# Revit family: Drain_Gutter_Zurn-Z575-Medium-Duty
name_source: partatom
category: Plumbing Fixtures
units: mm (PartAtom-declared; Revit-internal decimal feet)

## family parameters
Always vertical = Yes
Cut with Voids When Loaded = No
Maintain Annotation Orientation = No
OmniClass Number = 23.70.50.21.24.14
OmniClass Title = Deck Waste Water Drains
Part Type = Normal
Room Calculation Point = No
Round Connector Dimension = Use Radius
Shared = No
Work Plane-Based = No

## types (36) — shared parameters
Approx. Weight (Lbs) = 18 "
Assembly Code = D2030300
CW Connection = No
Default Elevation = 2 "
Description = 6 X 12 [152 X 305] MEDIUM-DUTY GUTTER DRAIN
Grate Open Area (Sq. In.) = 24 SF
HW Connection = No
Main Material = Iron - Zurn - Cast - Painted - Blue
Manufacturer = Zurn Water, LLC
Manufacurer Brand = Zurn
Model = Z575
Modified Date = 11/20/25
Product Documentation Link = https://files.zurn.com
Product Page URL = https://www.zurn.com
Product data url = https://www.bimobject.com
URL = www.zurn.com
Vent Connection = No
WFU = 1
Waste Connection = Yes
zero-valued in all types: CWFU, HWFU

## per-type parameters (varying)
| type | A_ Pipe Size (Inner Diameter) | A_ Pipe Size (Nominal Diameter) | A_ Pipe Size (Nominal Radius) | A_ Pipe Size (Outer Diameter) | Actual Body Height 'E' | Body Height 'E' | Grate Material | Thread length | Type Comments | Z1040-Adaptor Height | ZB/ZN | ZB/ZN Top |
| Z575-2IC | 2.067 " | 2 " | 1 " | 2.375 " | 5 " | 5 " | Iron - Zurn - Cast - Painted - Blue | 0 " | Z575 2 Inch Inside Caulk Outlet | 0 " | 0 " | No |
| Z575-3IC | 3.068 " | 3 " | 1.5 " | 3.5 " | 5 " | 5 " | Iron - Zurn - Cast - Painted - Blue | 0 " | Z575 3 Inch Inside Caulk Outlet | 0 " | 0 " | No |
| Z575-4IC | 4.026 " | 4 " | 2 " | 4.5 " | 5 " | 5 " | Iron - Zurn - Cast - Painted - Blue | 0 " | Z575 4 Inch Inside Caulk Outlet | 0 " | 0 " | No |
| ZB575-2IC | 2.067 " | 2 " | 1 " | 2.375 " | 5.188 " | 5 " | Bronze - Zurn - Polished | 0 " | ZB575 2 Inch Inside Caulk Outlet | 0 " | 0.188 " | Yes |
| ZB575-3IC | 3.068 " | 3 " | 1.5 " | 3.5 " | 5.188 " | 5 " | Bronze - Zurn - Polished | 0 " | ZB575 3 Inch Inside Caulk Outlet | 0 " | 0.188 " | Yes |
| ZB575-4IC | 4.026 " | 4 " | 2 " | 4.5 " | 5.188 " | 5 " | Bronze - Zurn - Polished | 0 " | ZB575 4 Inch Inside Caulk Outlet | 0 " | 0.188 " | Yes |
| ZN575-2IC | 2.067 " | 2 " | 1 " | 2.375 " | 5.188 " | 5 " | Bronze - Zurn - Polished Nickel | 0 " | ZN575 2 Inch Inside Caulk Outlet | 0 " | 0.188 " | Yes |
| ZN575-3IC | 3.068 " | 3 " | 1.5 " | 3.5 " | 5.188 " | 5 " | Bronze - Zurn - Polished Nickel | 0 " | ZN575 3 Inch Inside Caulk Outlet | 0 " | 0.188 " | Yes |
| ZN575-4IC | 4.026 " | 4 " | 2 " | 4.5 " | 5.188 " | 5 " | Bronze - Zurn - Polished Nickel | 0 " | ZN575 4 Inch Inside Caulk Outlet | 0 " | 0.188 " | Yes |
| Z575-2IP | 2.067 " | 2 " | 1 " | 2.375 " | 3.625 " | 3.625 " | Iron - Zurn - Cast - Painted - Blue | 0 " | Z575 2 Inch Threaded Outlet | 0 " | 0 " | No |
| Z575-3IP | 3.068 " | 3 " | 1.5 " | 3.5 " | 3.625 " | 3.625 " | Iron - Zurn - Cast - Painted - Blue | 0 " | Z575 3 Inch Threaded Outlet | 0 " | 0 " | No |
| Z575-4IP | 4.026 " | 4 " | 2 " | 4.5 " | 3.625 " | 3.625 " | Iron - Zurn - Cast - Painted - Blue | 0 " | Z575 4 Inch Threaded Outlet | 0 " | 0 " | No |
| ZB575-2IP | 2.067 " | 2 " | 1 " | 2.375 " | 3.813 " | 3.625 " | Bronze - Zurn - Polished | 0 " | ZB575 2 Inch Threaded Outlet | 0 " | 0.188 " | Yes |
| ZB575-3IP | 3.068 " | 3 " | 1.5 " | 3.5 " | 3.813 " | 3.625 " | Bronze - Zurn - Polished | 0 " | ZB575 3 Inch Threaded Outlet | 0 " | 0.188 " | Yes |
| ZB575-4IP | 4.026 " | 4 " | 2 " | 4.5 " | 3.813 " | 3.625 " | Bronze - Zurn - Polished | 0 " | ZB575 4 Inch Threaded Outlet | 0 " | 0.188 " | Yes |
| ZN575-2IP | 2.067 " | 2 " | 1 " | 2.375 " | 3.813 " | 3.625 " | Bronze - Zurn - Polished Nickel | 0 " | ZN575 2 Inch Threaded Outlet | 0 " | 0.188 " | Yes |
| ZN575-3IP | 3.068 " | 3 " | 1.5 " | 3.5 " | 3.813 " | 3.625 " | Bronze - Zurn - Polished Nickel | 0 " | ZN575 3 Inch Threaded Outlet | 0 " | 0.188 " | Yes |
| ZN575-4IP | 4.026 " | 4 " | 2 " | 4.5 " | 3.813 " | 3.625 " | Bronze - Zurn - Polished Nickel | 0 " | ZN575 4 Inch Threaded Outlet | 0 " | 0.188 " | Yes |
| Z575-2NH | 2.067 " | 2 " | 1 " | 2.375 " | 6.375 " | 3.625 " | Iron - Zurn - Cast - Painted - Blue | 0.75 " | Z575 2 Inch No-Hub Outlet (IP w//Z1040) | 3.5 " | 0 " | No |
| Z575-3NH | 3.068 " | 3 " | 1.5 " | 3.5 " | 6.125 " | 3.625 " | Iron - Zurn - Cast - Painted - Blue | 1 " | Z575 3 Inch No-Hub Outlet (IP w//Z1040) | 3.5 " | 0 " | No |
| Z575-4NH | 4.026 " | 4 " | 2 " | 4.5 " | 6 " | 3.625 " | Iron - Zurn - Cast - Painted - Blue | 1.125 " | Z575 4 Inch No-Hub Outlet (IP w//Z1040) | 3.5 " | 0 " | No |
| ZB575-2NH | 2.067 " | 2 " | 1 " | 2.375 " | 6.563 " | 3.625 " | Bronze - Zurn - Polished | 0.75 " | ZB575 2 Inch No-Hub Outlet (IP w//Z1040) | 3.5 " | 0.188 " | Yes |
| ZB575-3NH | 3.068 " | 3 " | 1.5 " | 3.5 " | 6.313 " | 3.625 " | Bronze - Zurn - Polished | 1 " | ZB575 3 Inch No-Hub Outlet (IP w//Z1040) | 3.5 " | 0.188 " | Yes |
| ZB575-4NH | 4.026 " | 4 " | 2 " | 4.5 " | 6.188 " | 3.625 " | Bronze - Zurn - Polished | 1.125 " | ZB575 4 Inch No-Hub Outlet (IP w//Z1040) | 3.5 " | 0.188 " | Yes |
| ZN575-2NH | 2.067 " | 2 " | 1 " | 2.375 " | 6.563 " | 3.625 " | Bronze - Zurn - Polished Nickel | 0.75 " | ZN575 2 Inch No-Hub Outlet (IP w//Z1040) | 3.5 " | 0.188 " | Yes |
| ZN575-3NH | 3.068 " | 3 " | 1.5 " | 3.5 " | 6.313 " | 3.625 " | Bronze - Zurn - Polished Nickel | 1 " | ZN575 3 Inch No-Hub Outlet (IP w//Z1040) | 3.5 " | 0.188 " | Yes |
| ZN575-4NH | 4.026 " | 4 " | 2 " | 4.5 " | 6.188 " | 3.625 " | Bronze - Zurn - Polished Nickel | 1.125 " | ZN575 4 Inch No-Hub Outlet (IP w//Z1040) | 3.5 " | 0.188 " | Yes |
| Z575-2NL | 2.067 " | 2 " | 1 " | 2.375 " | 4.5 " | 4.5 " | Iron - Zurn - Cast - Painted - Blue | 0 " | Z575 2 Inch Neo-Loc Outlet | 0 " | 0 " | No |
| Z575-3NL | 3.068 " | 3 " | 1.5 " | 3.5 " | 4.5 " | 4.5 " | Iron - Zurn - Cast - Painted - Blue | 0 " | Z575 3 Inch Neo-Loc Outlet | 0 " | 0 " | No |
| Z575-4NL | 4.026 " | 4 " | 2 " | 4.5 " | 4.5 " | 4.5 " | Iron - Zurn - Cast - Painted - Blue | 0 " | Z575 4 Inch Neo-Loc Outlet | 0 " | 0 " | No |
| ZB575-2NL | 2.067 " | 2 " | 1 " | 2.375 " | 4.688 " | 4.5 " | Bronze - Zurn - Polished | 0 " | ZB575 2 Inch Neo-Loc Outlet | 0 " | 0.188 " | Yes |
| ZB575-3NL | 3.068 " | 3 " | 1.5 " | 3.5 " | 4.688 " | 4.5 " | Bronze - Zurn - Polished | 0 " | ZB575 3 Inch Neo-Loc Outlet | 0 " | 0.188 " | Yes |
| ZB575-4NL | 4.026 " | 4 " | 2 " | 4.5 " | 4.688 " | 4.5 " | Bronze - Zurn - Polished | 0 " | ZB575 4 Inch Neo-Loc Outlet | 0 " | 0.188 " | Yes |
| ZN575-2NL | 2.067 " | 2 " | 1 " | 2.375 " | 4.688 " | 4.5 " | Bronze - Zurn - Polished Nickel | 0 " | ZN575 2 Inch Neo-Loc Outlet | 0 " | 0.188 " | Yes |
| ZN575-3NL | 3.068 " | 3 " | 1.5 " | 3.5 " | 4.688 " | 4.5 " | Bronze - Zurn - Polished Nickel | 0 " | ZN575 3 Inch Neo-Loc Outlet | 0 " | 0.188 " | Yes |
| ZN575-4NL | 4.026 " | 4 " | 2 " | 4.5 " | 4.688 " | 4.5 " | Bronze - Zurn - Polished Nickel | 0 " | ZN575 4 Inch Neo-Loc Outlet | 0 " | 0.188 " | Yes |

## geometry (parser evidence)
native form markers: Blend x10, Sweep x22
no freeform markers — native parametric forms only
